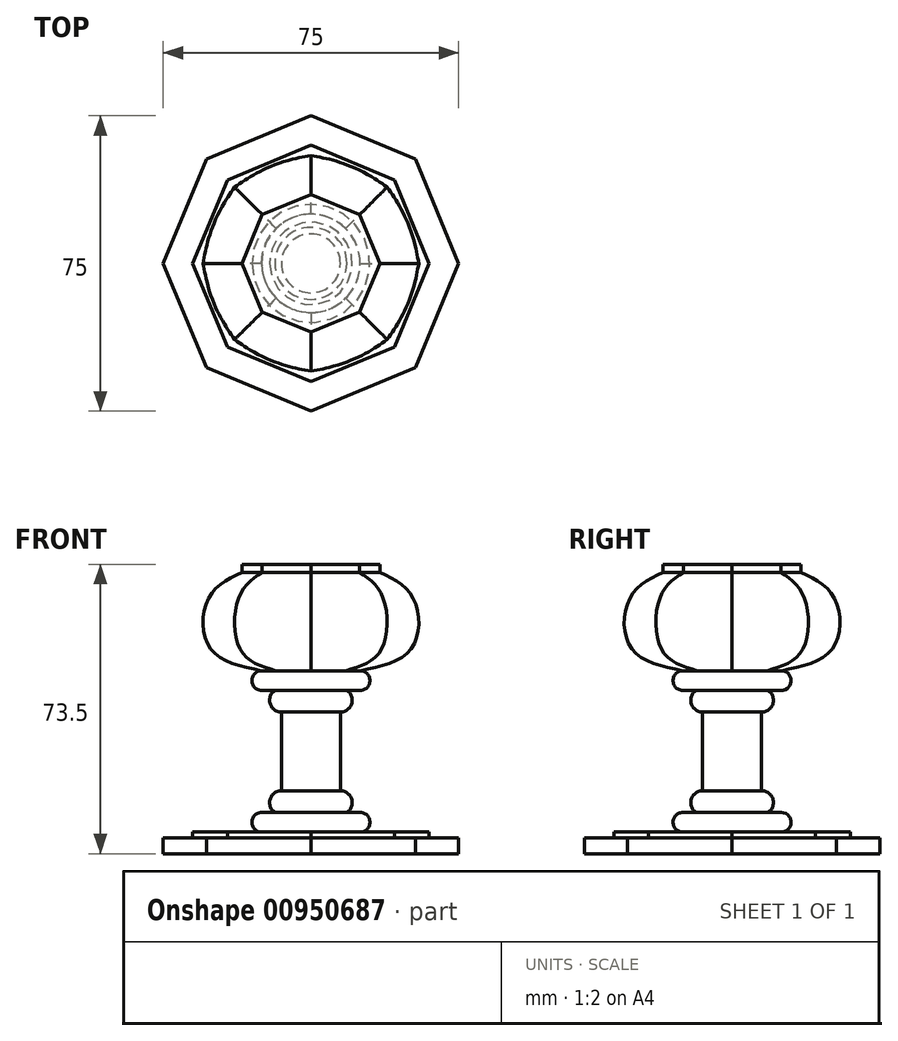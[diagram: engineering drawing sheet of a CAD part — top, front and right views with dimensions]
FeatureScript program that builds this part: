
annotation { "Feature Type Name" : "Feature", "Feature Type Description" : "" }
export const myFeature = defineFeature(function(context is Context, id is Id, definition is map)
    precondition{}
    {
        {
            var Q0;
            Q0=qCreatedBy(makeId("Top.planeOp"),FACE);
            var sketch = newSketch(context, id + "F0", { "sketchPlane" : qUnion([Q0])});
            skCircle(sketch, "E0.cCircle", {"center": v(0, 0) * mm, "radius": 37.5 * mm, "construction": true});
            skLineSegment(sketch, "E0.0", {"start": v(37.5, 0) * mm, "end": v(26.52, -26.52) * mm});
            skLineSegment(sketch, "E0.1", {"start": v(26.52, -26.52) * mm, "end": v(0, -37.5) * mm});
            skLineSegment(sketch, "E0.2", {"start": v(0, -37.5) * mm, "end": v(-26.52, -26.52) * mm});
            skLineSegment(sketch, "E0.3", {"start": v(-26.52, -26.52) * mm, "end": v(-37.5, 0) * mm});
            skLineSegment(sketch, "E0.4", {"start": v(-37.5, 0) * mm, "end": v(-26.52, 26.52) * mm});
            skLineSegment(sketch, "E0.5", {"start": v(-26.52, 26.52) * mm, "end": v(0, 37.5) * mm});
            skLineSegment(sketch, "E0.6", {"start": v(0, 37.5) * mm, "end": v(26.52, 26.52) * mm});
            skLineSegment(sketch, "E0.7", {"start": v(26.52, 26.52) * mm, "end": v(37.5, 0) * mm});
            skSolve(sketch);
        }
        {
            var Q0;
            Q0=makeQuery(id+"F0.imprint","IMPRINT",FACE,{"disambiguationData":[TD([[makeQuery(id+"F0.imprint","IMPRINT",EDGE,{"derivedFrom":sQuery(id+"F0.wireOp",EDGE,"E0.0")}),-1.0]])]});
            extrude(context, id + "F1", {"entities" : qUnion([Q0]), "depth" : 4 * mm, "offsetDistance" : 25 * mm});
        }
        {
            var Q0;
            Q0=makeQuery(id+"F1.opExtrude","CAP_FACE",FACE,{"disambiguationData":[OSD([sQuery(id+"F0.wireOp",EDGE,"E0.0"),sQuery(id+"F0.wireOp",EDGE,"E0.1"),sQuery(id+"F0.wireOp",EDGE,"E0.2"),sQuery(id+"F0.wireOp",EDGE,"E0.3"),sQuery(id+"F0.wireOp",EDGE,"E0.4"),sQuery(id+"F0.wireOp",EDGE,"E0.5"),sQuery(id+"F0.wireOp",EDGE,"E0.6"),sQuery(id+"F0.wireOp",EDGE,"E0.7")])],"isStart":false});
            var sketch = newSketch(context, id + "F2", { "sketchPlane" : qUnion([Q0])});
            skCircle(sketch, "E1.cCircle", {"center": v(0, 0) * mm, "radius": 30 * mm, "construction": true});
            skLineSegment(sketch, "E1.0", {"start": v(30, 0) * mm, "end": v(21.21, -21.21) * mm});
            skLineSegment(sketch, "E1.1", {"start": v(21.21, -21.21) * mm, "end": v(0, -30) * mm});
            skLineSegment(sketch, "E1.2", {"start": v(0, -30) * mm, "end": v(-21.21, -21.21) * mm});
            skLineSegment(sketch, "E1.3", {"start": v(-21.21, -21.21) * mm, "end": v(-30, 0) * mm});
            skLineSegment(sketch, "E1.4", {"start": v(-30, 0) * mm, "end": v(-21.21, 21.21) * mm});
            skLineSegment(sketch, "E1.5", {"start": v(-21.21, 21.21) * mm, "end": v(0, 30) * mm});
            skLineSegment(sketch, "E1.6", {"start": v(0, 30) * mm, "end": v(21.21, 21.21) * mm});
            skLineSegment(sketch, "E1.7", {"start": v(21.21, 21.21) * mm, "end": v(30, 0) * mm});
            skSolve(sketch);
        }
        {
            var Q0;
            Q0=makeQuery(id+"F2.imprint","IMPRINT",FACE,{"disambiguationData":[TD([[makeQuery(id+"F2.imprint","IMPRINT",EDGE,{"derivedFrom":sQuery(id+"F2.wireOp",EDGE,"E1.0")}),-1.0]])]});
            extrude(context, id + "F3", {"entities" : qUnion([Q0]), "operationType" : NewBodyOperationType.ADD, "depth" : 1.5 * mm, "offsetDistance" : 25 * mm});
        }
        {
            var Q0;
            Q0=qCreatedBy(makeId("Front.planeOp"),FACE);
            var sketch = newSketch(context, id + "F4", { "sketchPlane" : qUnion([Q0])});
            skLineSegment(sketch, "E2", {"start": v(0, 0) * mm, "end": v(0, 93.5) * mm, "construction": true});
            skLineSegment(sketch, "E3", {"start": v(7.5, 36) * mm, "end": v(7.5, 16) * mm});
            skLineSegment(sketch, "E4", {"start": v(12.5, 5.5) * mm, "end": v(0, 5.5) * mm});
            skLineSegment(sketch, "E5", {"start": v(7.5, 26) * mm, "end": v(0, 26) * mm, "construction": true});
            skLineSegment(sketch, "E6", {"start": v(0, 5.5) * mm, "end": v(0, 46.5) * mm});
            skLineSegment(sketch, "E7", {"start": v(9.16, 10.5) * mm, "end": v(12.5, 10.5) * mm});
            skArc(sketch, "E8", {"start": v(12.5, 5.5) * mm, "mid": v(15, 8) * mm, "end": v(12.5, 10.5) * mm});
            skArc(sketch, "E9", {"start": v(9.16, 10.5) * mm, "mid": v(10.37, 13.87) * mm, "end": v(7.5, 16) * mm});
            skArc(sketch, "E10.MirrorCS", {"start": v(9.16, 41.5) * mm, "mid": v(10.37, 38.13) * mm, "end": v(7.5, 36) * mm});
            skLineSegment(sketch, "E11.MirrorCS", {"start": v(9.16, 41.5) * mm, "end": v(12.5, 41.5) * mm});
            skArc(sketch, "E12.MirrorCS", {"start": v(12.5, 46.5) * mm, "mid": v(15, 44) * mm, "end": v(12.5, 41.5) * mm});
            skLineSegment(sketch, "E13", {"start": v(0, 46.5) * mm, "end": v(12.5, 46.5) * mm});
            skSolve(sketch);
        }
        {
            var Q0;
            Q0=makeQuery(id+"F4.imprint","IMPRINT",FACE,{"disambiguationData":[TD([[makeQuery(id+"F4.imprint","IMPRINT",EDGE,{"derivedFrom":sQuery(id+"F4.wireOp",EDGE,"E3")}),-1.0]])]});
            var Q1;
            Q1=sQuery(id+"F4.wireOp",EDGE,"E2");
            revolve(context, id + "F5", {"operationType" : NewBodyOperationType.ADD, "surfaceOperationType" : NewSurfaceOperationType.NEW, "entities" : qUnion([Q0]), "axis" : qUnion([Q1]), "revolveType" : RevolveType.FULL});
        }
        {
            var Q0;
            Q0=makeQuery(id+"F5.opRevolve","SWEPT_FACE",FACE,{"disambiguationData":[OSD([sQuery(id+"F4.wireOp",EDGE,"E13")])]});
            var sketch = newSketch(context, id + "F6", { "sketchPlane" : qUnion([Q0])});
            skCircle(sketch, "E14.0", {"center": v(0, 0) * mm, "radius": 12.5 * mm});
            skSolve(sketch);
        }
        {
            var Q0;
            Q0=makeQuery(id+"F5.opRevolve","SWEPT_FACE",FACE,{"disambiguationData":[OSD([sQuery(id+"F4.wireOp",EDGE,"E13")])]});
            cPlane(context, id + "F7", {"entities" : qUnion([Q0]), "cplaneType" : CPlaneType.OFFSET, "offset" : 5 * mm, "width" : 150 * mm, "height" : 150 * mm});
        }
        {
            var Q0;
            Q0=qCreatedBy(id+"F7.planeOp",FACE);
            var sketch = newSketch(context, id + "F8", { "sketchPlane" : qUnion([Q0])});
            skCircle(sketch, "E15.cCircle", {"center": v(0, 0) * mm, "radius": 25 * mm, "construction": true});
            skLineSegment(sketch, "E15.0", {"start": v(25, 0) * mm, "end": v(17.68, -17.68) * mm});
            skLineSegment(sketch, "E15.1", {"start": v(17.68, -17.68) * mm, "end": v(0, -25) * mm});
            skLineSegment(sketch, "E15.2", {"start": v(0, -25) * mm, "end": v(-17.68, -17.68) * mm});
            skLineSegment(sketch, "E15.3", {"start": v(-17.68, -17.68) * mm, "end": v(-25, 0) * mm});
            skLineSegment(sketch, "E15.4", {"start": v(-25, 0) * mm, "end": v(-17.68, 17.68) * mm});
            skLineSegment(sketch, "E15.5", {"start": v(-17.68, 17.68) * mm, "end": v(0, 25) * mm});
            skLineSegment(sketch, "E15.6", {"start": v(0, 25) * mm, "end": v(17.68, 17.68) * mm});
            skLineSegment(sketch, "E15.7", {"start": v(17.68, 17.68) * mm, "end": v(25, 0) * mm});
            skSolve(sketch);
        }
        {
            var Q0;
            Q0=qCreatedBy(id+"F7.planeOp",FACE);
            cPlane(context, id + "F9", {"entities" : qUnion([Q0]), "cplaneType" : CPlaneType.OFFSET, "offset" : 15 * mm, "width" : 150 * mm, "height" : 150 * mm});
        }
        {
            var Q0;
            Q0=qCreatedBy(id+"F9.planeOp",FACE);
            var sketch = newSketch(context, id + "F10", { "sketchPlane" : qUnion([Q0])});
            skCircle(sketch, "E16.0", {"center": v(0, 0) * mm, "radius": 25 * mm});
            skLineSegment(sketch, "E16.1", {"start": v(25, 0) * mm, "end": v(17.68, -17.68) * mm});
            skLineSegment(sketch, "E16.2", {"start": v(17.68, -17.68) * mm, "end": v(0, -25) * mm});
            skLineSegment(sketch, "E16.3", {"start": v(0, -25) * mm, "end": v(-17.68, -17.68) * mm});
            skLineSegment(sketch, "E16.4", {"start": v(-17.68, -17.68) * mm, "end": v(-25, 0) * mm});
            skLineSegment(sketch, "E16.5", {"start": v(-25, 0) * mm, "end": v(-17.68, 17.68) * mm});
            skLineSegment(sketch, "E16.6", {"start": v(-17.68, 17.68) * mm, "end": v(0, 25) * mm});
            skLineSegment(sketch, "E16.7", {"start": v(0, 25) * mm, "end": v(17.68, 17.68) * mm});
            skLineSegment(sketch, "E16.8", {"start": v(17.68, 17.68) * mm, "end": v(25, 0) * mm});
            skSolve(sketch);
        }
        {
            var Q0;
            Q0=qCreatedBy(id+"F9.planeOp",FACE);
            cPlane(context, id + "F11", {"entities" : qUnion([Q0]), "cplaneType" : CPlaneType.OFFSET, "offset" : 5 * mm, "width" : 150 * mm, "height" : 150 * mm});
        }
        {
            var Q0;
            Q0=qCreatedBy(id+"F11.planeOp",FACE);
            var sketch = newSketch(context, id + "F12", { "sketchPlane" : qUnion([Q0])});
            skCircle(sketch, "E17.cCircle", {"center": v(0, 0) * mm, "radius": 17.5 * mm, "construction": true});
            skLineSegment(sketch, "E17.0", {"start": v(17.5, 0) * mm, "end": v(12.37, -12.37) * mm});
            skLineSegment(sketch, "E17.1", {"start": v(12.37, -12.37) * mm, "end": v(0, -17.5) * mm});
            skLineSegment(sketch, "E17.2", {"start": v(0, -17.5) * mm, "end": v(-12.37, -12.37) * mm});
            skLineSegment(sketch, "E17.3", {"start": v(-12.37, -12.37) * mm, "end": v(-17.5, 0) * mm});
            skLineSegment(sketch, "E17.4", {"start": v(-17.5, 0) * mm, "end": v(-12.37, 12.37) * mm});
            skLineSegment(sketch, "E17.5", {"start": v(-12.37, 12.37) * mm, "end": v(0, 17.5) * mm});
            skLineSegment(sketch, "E17.6", {"start": v(0, 17.5) * mm, "end": v(12.37, 12.37) * mm});
            skLineSegment(sketch, "E17.7", {"start": v(12.37, 12.37) * mm, "end": v(17.5, 0) * mm});
            skSolve(sketch);
        }
        {
            var Q1;
            Q1=qSketchRegion(id+"F6",true);
            var Q2;
            Q2=qSketchRegion(id+"F8",true);
            var Q3;
            Q3=qSketchRegion(id+"F10",true);
            var Q4;
            Q4=qSketchRegion(id+"F12",true);
            loft(context, id + "F13", {"operationType" : NewBodyOperationType.ADD, "sheetProfilesArray" : [{ "sheetProfileEntities" : qUnion([Q1]) }, { "sheetProfileEntities" : qUnion([Q2]) }, { "sheetProfileEntities" : qUnion([Q3]) }, { "sheetProfileEntities" : qUnion([Q4]) }]});
        }
        {
            var Q0;
            Q0=makeQuery(id+"F13.opLoft","CAP_FACE",FACE,{"disambiguationData":[OSD([makeQuery(id+"F12.imprint","IMPRINT",FACE,{"disambiguationData":[TD([[makeQuery(id+"F12.imprint","IMPRINT",EDGE,{"derivedFrom":sQuery(id+"F12.wireOp",EDGE,"E17.0")}),-1.0]])]})])],"isStart":true});
            extrude(context, id + "F14", {"entities" : qUnion([Q0]), "operationType" : NewBodyOperationType.ADD, "depth" : 2 * mm, "offsetDistance" : 25 * mm});
        }
    });
